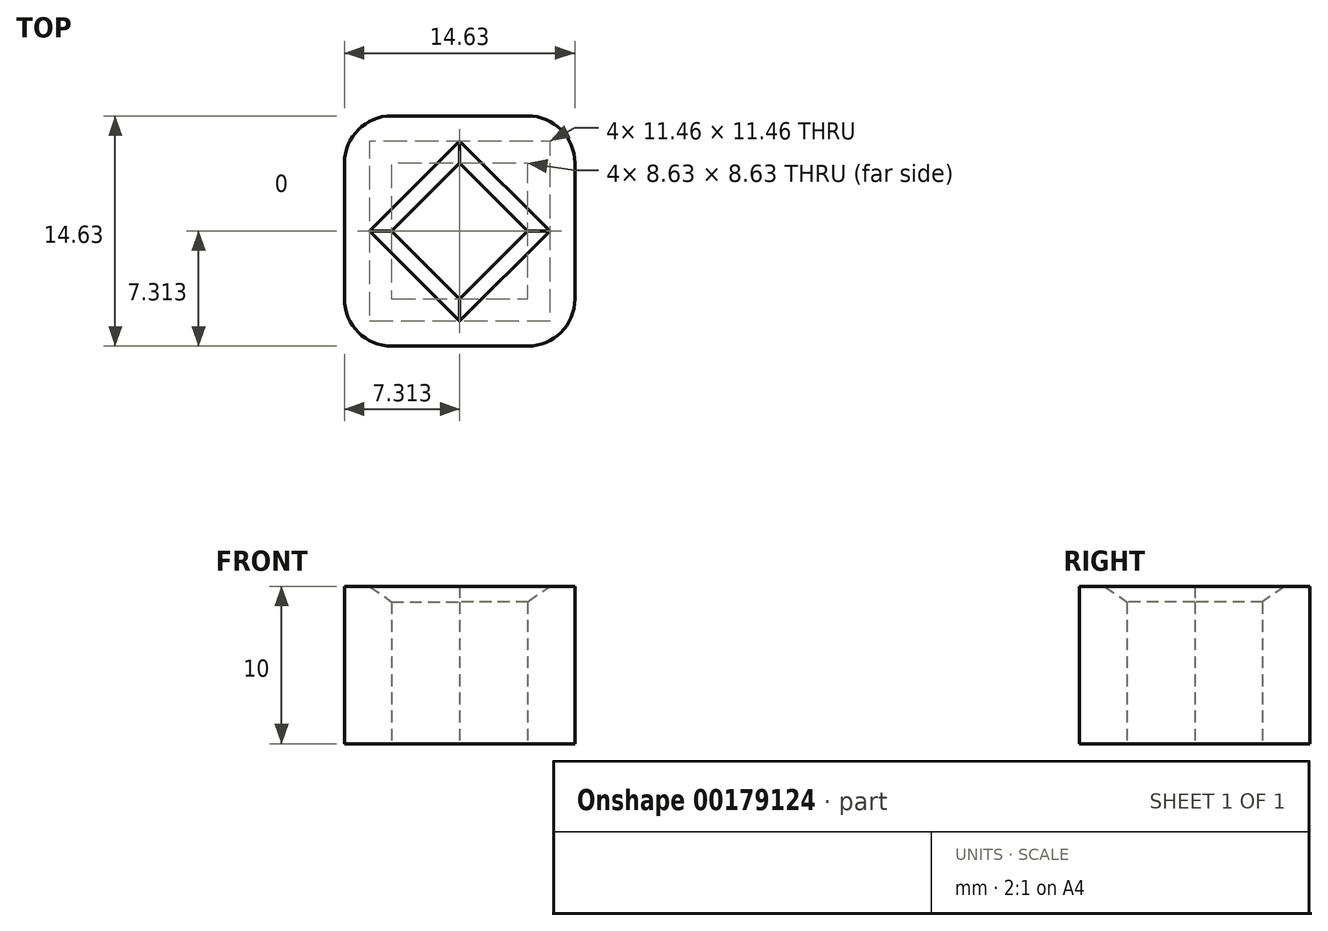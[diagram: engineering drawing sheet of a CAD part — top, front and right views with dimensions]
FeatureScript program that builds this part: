
annotation { "Feature Type Name" : "Feature", "Feature Type Description" : "" }
export const myFeature = defineFeature(function(context is Context, id is Id, definition is map)
    precondition{}
    {
        {
            var Q0;
            Q0=qCreatedBy(makeId("Top.planeOp"),FACE);
            var sketch = newSketch(context, id + "F0", { "sketchPlane" : qUnion([Q0])});
            skLineSegment(sketch, "E0.bottom", {"start": v(0, 0) * mm, "end": v(14.63, 0) * mm});
            skLineSegment(sketch, "E0.top", {"start": v(0, 14.63) * mm, "end": v(14.63, 14.63) * mm});
            skLineSegment(sketch, "E0.left", {"start": v(0, 0) * mm, "end": v(0, 14.63) * mm});
            skLineSegment(sketch, "E0.right", {"start": v(14.63, 0) * mm, "end": v(14.63, 14.63) * mm});
            skLineSegment(sketch, "E1", {"start": v(0, 7.31) * mm, "end": v(14.63, 7.31) * mm});
            skLineSegment(sketch, "E2", {"start": v(7.31, 14.63) * mm, "end": v(7.31, 0) * mm});
            skLineSegment(sketch, "E3", {"start": v(3, 7.31) * mm, "end": v(7.31, 3) * mm});
            skLineSegment(sketch, "E4", {"start": v(7.31, 3) * mm, "end": v(11.63, 7.31) * mm});
            skLineSegment(sketch, "E5", {"start": v(11.63, 7.31) * mm, "end": v(7.31, 11.63) * mm});
            skLineSegment(sketch, "E6", {"start": v(7.31, 11.63) * mm, "end": v(3, 7.31) * mm});
            skSolve(sketch);
        }
        {
            var Q0;
            {var subQ3=sQuery(id+"F0.wireOp",EDGE,"E6");Q0=makeQuery(id+"F0.imprint","IMPRINT",FACE,{"disambiguationData":[TD([[makeQuery(id+"F0.imprint","IMPRINT",EDGE,{"derivedFrom":subQ3}),-1.0]])]});}
            var Q1;
            {var subQ3=sQuery(id+"F0.wireOp",EDGE,"E3");Q1=makeQuery(id+"F0.imprint","IMPRINT",FACE,{"disambiguationData":[TD([[makeQuery(id+"F0.imprint","IMPRINT",EDGE,{"derivedFrom":subQ3}),-1.0]])]});}
            var Q2;
            {var subQ3=sQuery(id+"F0.wireOp",EDGE,"E4");Q2=makeQuery(id+"F0.imprint","IMPRINT",FACE,{"disambiguationData":[TD([[makeQuery(id+"F0.imprint","IMPRINT",EDGE,{"derivedFrom":subQ3}),-1.0]])]});}
            var Q3;
            {var subQ3=sQuery(id+"F0.wireOp",EDGE,"E5");Q3=makeQuery(id+"F0.imprint","IMPRINT",FACE,{"disambiguationData":[TD([[makeQuery(id+"F0.imprint","IMPRINT",EDGE,{"derivedFrom":subQ3}),-1.0]])]});}
            extrude(context, id + "F1", {"entities" : qUnion([Q0, Q1, Q2, Q3]), "depth" : 10 * mm});
        }
        {
            var Q0;
            Q0=makeQuery(id+"F1.opExtrude","SWEPT_EDGE",EDGE,{"disambiguationData":[OSD([sQuery(id+"F0.wireOp",EDGE,"E0.bottom"),sQuery(id+"F0.wireOp",EDGE,"E0.left")])]});
            var Q1;
            Q1=makeQuery(id+"F1.opExtrude","SWEPT_EDGE",EDGE,{"disambiguationData":[OSD([sQuery(id+"F0.wireOp",EDGE,"E0.top"),sQuery(id+"F0.wireOp",EDGE,"E0.left")])]});
            var Q2;
            Q2=makeQuery(id+"F1.opExtrude","SWEPT_EDGE",EDGE,{"disambiguationData":[OSD([sQuery(id+"F0.wireOp",EDGE,"E0.bottom"),sQuery(id+"F0.wireOp",EDGE,"E0.right")])]});
            var Q3;
            Q3=makeQuery(id+"F1.opExtrude","SWEPT_EDGE",EDGE,{"disambiguationData":[OSD([sQuery(id+"F0.wireOp",EDGE,"E0.top"),sQuery(id+"F0.wireOp",EDGE,"E0.right")])]});
            fillet(context, id + "F2", {"entities" : qUnion([Q0, Q1, Q2, Q3]), "radius" : 3 * mm, "tangentPropagation" : true, "allowEdgeOverflow" : false});
        }
        {
            var Q0;
            Q0=makeQuery(id+"F1.opExtrude","CAP_EDGE",EDGE,{"disambiguationData":[OSD([sQuery(id+"F0.wireOp",EDGE,"E6")])],"isStart":false});
            var Q1;
            Q1=makeQuery(id+"F1.opExtrude","CAP_EDGE",EDGE,{"disambiguationData":[OSD([sQuery(id+"F0.wireOp",EDGE,"E3")])],"isStart":false});
            var Q2;
            Q2=makeQuery(id+"F1.opExtrude","CAP_EDGE",EDGE,{"disambiguationData":[OSD([sQuery(id+"F0.wireOp",EDGE,"E5")])],"isStart":false});
            var Q3;
            Q3=makeQuery(id+"F1.opExtrude","CAP_EDGE",EDGE,{"disambiguationData":[OSD([sQuery(id+"F0.wireOp",EDGE,"E4")])],"isStart":false});
            chamfer(context, id + "F3", {"entities" : qUnion([Q0, Q1, Q2, Q3]), "width" : 1 * mm, "tangentPropagation" : true});
        }
    });
